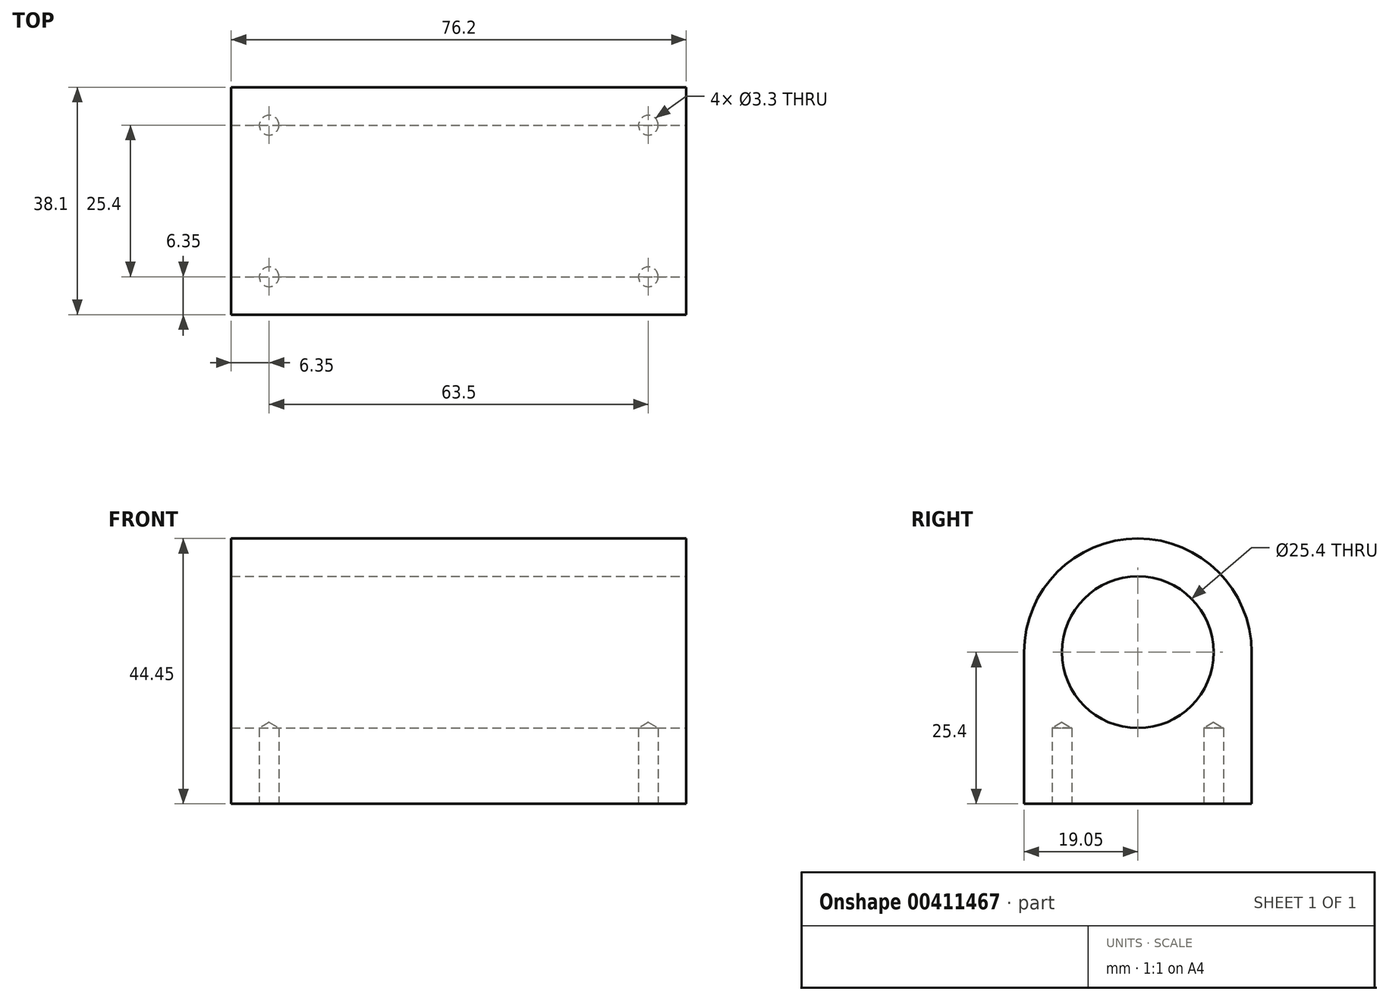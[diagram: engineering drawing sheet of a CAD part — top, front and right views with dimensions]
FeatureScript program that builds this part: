
annotation { "Feature Type Name" : "Feature", "Feature Type Description" : "" }
export const myFeature = defineFeature(function(context is Context, id is Id, definition is map)
    precondition{}
    {
        {
            var Q0;
            Q0=qCreatedBy(makeId("Right.planeOp"),FACE);
            var sketch = newSketch(context, id + "F0", { "sketchPlane" : qUnion([Q0])});
            skArc(sketch, "E0", {"start": v(-19.05, 0) * mm, "mid": v(0, 19.05) * mm, "end": v(19.05, 0) * mm});
            skLineSegment(sketch, "E1", {"start": v(-19.05, 0) * mm, "end": v(-19.05, -25.4) * mm});
            skLineSegment(sketch, "E2", {"start": v(-19.05, -25.4) * mm, "end": v(19.05, -25.4) * mm});
            skLineSegment(sketch, "E3", {"start": v(19.05, -25.4) * mm, "end": v(19.05, 0) * mm});
            skSolve(sketch);
        }
        {
            var Q0;
            Q0 = qSketchRegion(id + "F0", true);
            extrude(context, id + "F1", {"entities" : qUnion([Q0]), "endBound" : BoundingType.SYMMETRIC, "depth" : 76.2 * mm});
        }
        {
            var Q0;
            Q0=makeQuery(id+"F1.opExtrude","CAP_FACE",FACE,{"disambiguationData":[OSD([sQuery(id+"F0.wireOp",EDGE,"E0"),sQuery(id+"F0.wireOp",EDGE,"E1"),sQuery(id+"F0.wireOp",EDGE,"E2"),sQuery(id+"F0.wireOp",EDGE,"E3")])],"isStart":false});
            var sketch = newSketch(context, id + "F2", { "sketchPlane" : qUnion([Q0])});
            skCircle(sketch, "E4", {"center": v(0, 0) * mm, "radius": 12.7 * mm});
            skSolve(sketch);
        }
        {
            var Q0;
            Q0 = qSketchRegion(id + "F2", true);
            extrude(context, id + "F3", {"entities" : qUnion([Q0]), "operationType" : NewBodyOperationType.REMOVE, "endBound" : BoundingType.THROUGH_ALL, "oppositeDirection" : true, "depth" : 25.4 * mm});
        }
        {
            var Q0;
            Q0=makeQuery(id+"F1.opExtrude","SWEPT_FACE",FACE,{"disambiguationData":[OSD([sQuery(id+"F0.wireOp",EDGE,"E2")])]});
            var sketch = newSketch(context, id + "F4", { "sketchPlane" : qUnion([Q0])});
            skLineSegment(sketch, "E5.bottom", {"start": v(-31.75, 12.7) * mm, "end": v(31.75, 12.7) * mm, "construction": true});
            skLineSegment(sketch, "E5.top", {"start": v(-31.75, -12.7) * mm, "end": v(31.75, -12.7) * mm, "construction": true});
            skLineSegment(sketch, "E5.left", {"start": v(-31.75, 12.7) * mm, "end": v(-31.75, -12.7) * mm, "construction": true});
            skLineSegment(sketch, "E5.right", {"start": v(31.75, 12.7) * mm, "end": v(31.75, -12.7) * mm, "construction": true});
            skPoint(sketch, "E5.middle", {"position": v(0, 0) * mm});
            skSolve(sketch);
        }
        {
            var Q0;
            Q0=sQuery(id+"F4.wireOp",VERTEX,"E5.left.start");
            var Q1;
            Q1=sQuery(id+"F4.wireOp",VERTEX,"E5.left.end");
            var Q2;
            Q2=sQuery(id+"F4.wireOp",VERTEX,"E5.top.end");
            var Q3;
            Q3=sQuery(id+"F4.wireOp",VERTEX,"E5.right.start");
            var Q4;
            Q4=makeQuery(id+"F1.opExtrude","SWEPT_BODY",BODY,{"disambiguationData":[OSD([sQuery(id+"F0.wireOp",EDGE,"E0"),sQuery(id+"F0.wireOp",EDGE,"E1"),sQuery(id+"F0.wireOp",EDGE,"E2"),sQuery(id+"F0.wireOp",EDGE,"E3")])]});
            hole(context, id + "F5", {"style" : HoleStyle.SIMPLE, "endStyle" : HoleEndStyle.BLIND, "holeDiameter" : 3.3 * mm, "holeDepth" : 12.7 * mm, "isTappedThrough" : true, "tappedDepth" : 12.7 * mm, "tapClearance" : 3, "locations" : qUnion([Q0, Q1, Q2, Q3]), "scope" : qUnion([Q4])});
        }
    });
